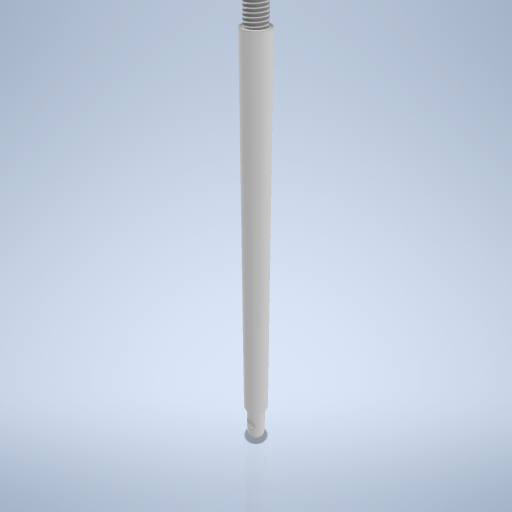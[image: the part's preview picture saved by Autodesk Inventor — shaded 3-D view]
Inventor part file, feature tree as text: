
AUTODESK INVENTOR PART (.ipt)
format: ipt  version: 2024.2 (Build 282272000, 272)  size: 260,096 bytes
history: native  units: mm
features: sketch x2, revolve x1, thread x1, plane x1, hole x1
ambient origin geometry x8: Origin, YZ Plane, XZ Plane, XY Plane, X Axis, Y Axis, Z Axis, Center Point
bodies: Volumenkörper1 (feature_tree)
feature tree (6):
  revolve  "Umdrehung1"
  thread  "Gewinde1"  [1 undecoded]
  plane  "Arbeitsebene1"
  hole  "Bohrung1"  [1 undecoded]
  sketch  "Skizze1"  dims[d1=3.0mm d2=4.0mm]
  sketch  "Skizze2"  dims[d5=61.5mm d6=0.5mm d7=6.0mm d9=90.0deg d10=18.0mm d11=0.0mm d12=1.75mm d13=3.5mm d14=2.0mm d15=6.0mm d16=4.0mm d17=2.0mm d18=90.0deg d19=8.0mm d20=0.0mm]
note: 2 required parameter values undecoded (feature->parameter linkage not recoverable at this tier; creation-order binding heuristic only, values carry confidence <= 0.55)
